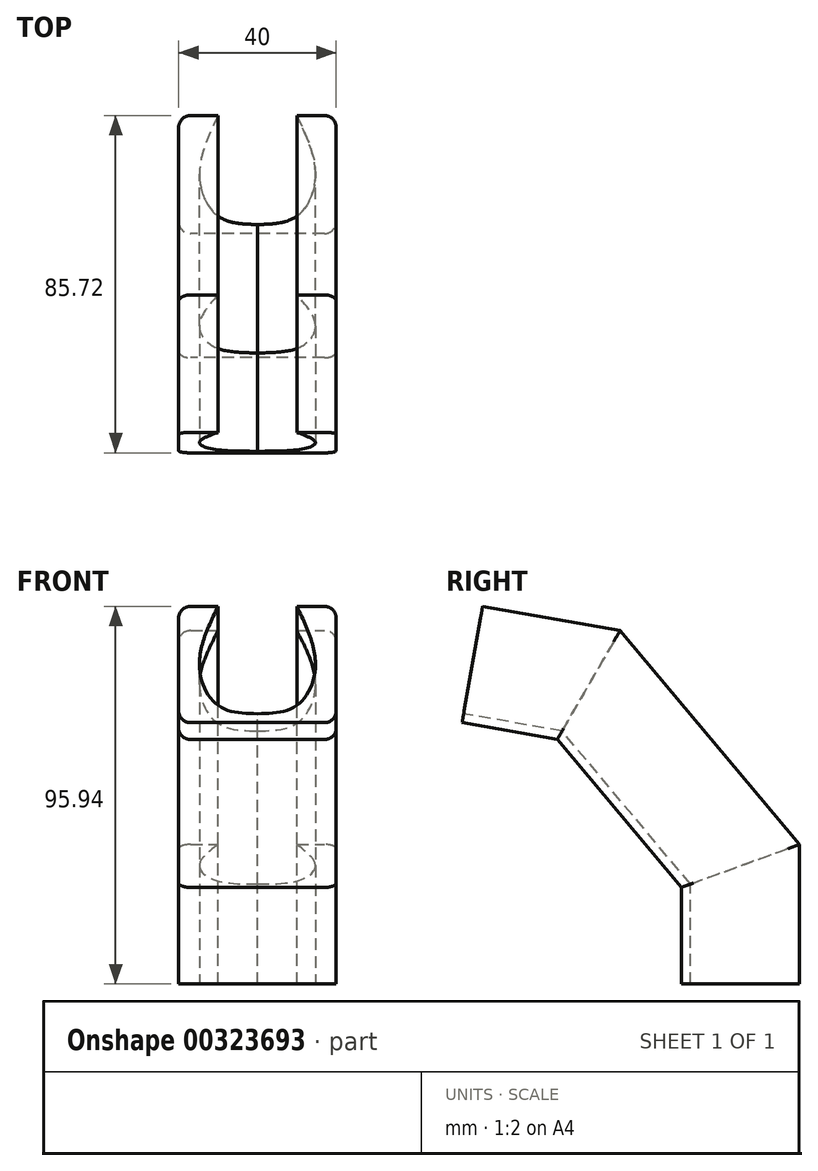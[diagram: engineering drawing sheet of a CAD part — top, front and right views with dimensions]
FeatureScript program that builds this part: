
annotation { "Feature Type Name" : "Feature", "Feature Type Description" : "" }
export const myFeature = defineFeature(function(context is Context, id is Id, definition is map)
    precondition{}
    {
        {
            var Q0;
            Q0=qCreatedBy(makeId("Top.planeOp"),FACE);
            var sketch = newSketch(context, id + "F0", { "sketchPlane" : qUnion([Q0])});
            skLineSegment(sketch, "E0.bottom", {"start": v(20, 15) * mm, "end": v(10, 15) * mm});
            skLineSegment(sketch, "E0.top", {"start": v(20, -15) * mm, "end": v(-20, -15) * mm});
            skLineSegment(sketch, "E0.left", {"start": v(20, 15) * mm, "end": v(20, -15) * mm});
            skLineSegment(sketch, "E0.right", {"start": v(-20, 15) * mm, "end": v(-20, -15) * mm});
            skPoint(sketch, "E0.middle", {"position": v(0, 0) * mm});
            skPoint(sketch, "E1", {"position": v(-10, 15) * mm});
            skPoint(sketch, "E2", {"position": v(10, 15) * mm});
            skFitSpline(sketch, "E3", {"points": [v(-10, 15) * mm, v(-14.75, 0) * mm, v(-10, -10.55) * mm, v(0, -12.7) * mm], "startDerivative": vector(-19.13, -40.12) * mm, "endDerivative": vector(36.12, -0.91) * mm});
            skFitSpline(sketch, "E4.MirrorCS", {"points": [v(10, 15) * mm, v(14.75, 0) * mm, v(10, -10.55) * mm, v(0, -12.7) * mm], "startDerivative": vector(19.13, -40.12) * mm, "endDerivative": vector(-36.12, -0.91) * mm});
            skLineSegment(sketch, "E5.trimOffspring", {"start": v(-10, 15) * mm, "end": v(-20, 15) * mm});
            skSolve(sketch);
        }
        {
            var Q0;
            Q0=qCreatedBy(makeId("Right.planeOp"),FACE);
            var sketch = newSketch(context, id + "F1", { "sketchPlane" : qUnion([Q0])});
            skLineSegment(sketch, "E6", {"start": v(0, 0) * mm, "end": v(0, 30) * mm});
            skLineSegment(sketch, "E7", {"start": v(0, 30) * mm, "end": v(-38.57, 75.96) * mm});
            skLineSegment(sketch, "E8", {"start": v(-38.57, 75.96) * mm, "end": v(-68.11, 81.17) * mm});
            skSolve(sketch);
        }
        {
            var Q0;
            Q0=makeQuery(id+"F0.imprint","IMPRINT",FACE,{"disambiguationData":[TD([[makeQuery(id+"F0.imprint","IMPRINT",EDGE,{"derivedFrom":sQuery(id+"F0.wireOp",EDGE,"E0.bottom")}),1.0]])]});
            var Q1;
            Q1=sQuery(id+"F1.wireOp",EDGE,"E6");
            var Q2;
            Q2=sQuery(id+"F1.wireOp",EDGE,"E7");
            var Q3;
            Q3=sQuery(id+"F1.wireOp",EDGE,"E8");
            sweep(context, id + "F2", {"profiles" : qUnion([Q0]), "path" : qUnion([Q1, Q2, Q3])});
        }
        {
            var Q0;
            Q0=makeQuery(id+"F2.opSweep","SWEPT_EDGE",EDGE,{"disambiguationData":[OSD([sQuery(id+"F0.wireOp",EDGE,"E0.right"),sQuery(id+"F0.wireOp",EDGE,"E5.trimOffspring"),sQuery(id+"F1.wireOp",EDGE,"E6")])]});
            var Q1;
            Q1=makeQuery(id+"F2.opSweep","SWEPT_EDGE",EDGE,{"disambiguationData":[OSD([sQuery(id+"F0.wireOp",EDGE,"E0.right"),sQuery(id+"F0.wireOp",EDGE,"E5.trimOffspring"),sQuery(id+"F1.wireOp",EDGE,"E7")])]});
            var Q2;
            Q2=makeQuery(id+"F2.opSweep","SWEPT_EDGE",EDGE,{"disambiguationData":[OSD([sQuery(id+"F0.wireOp",EDGE,"E0.right"),sQuery(id+"F0.wireOp",EDGE,"E5.trimOffspring"),sQuery(id+"F1.wireOp",EDGE,"E8")])]});
            var Q3;
            Q3=makeQuery(id+"F2.opSweep","SWEPT_EDGE",EDGE,{"disambiguationData":[OSD([sQuery(id+"F0.wireOp",EDGE,"E0.top"),sQuery(id+"F0.wireOp",EDGE,"E0.right"),sQuery(id+"F1.wireOp",EDGE,"E6")])]});
            var Q4;
            Q4=makeQuery(id+"F2.opSweep","SWEPT_EDGE",EDGE,{"disambiguationData":[OSD([sQuery(id+"F0.wireOp",EDGE,"E0.top"),sQuery(id+"F0.wireOp",EDGE,"E0.right"),sQuery(id+"F1.wireOp",EDGE,"E7")])]});
            var Q5;
            Q5=makeQuery(id+"F2.opSweep","SWEPT_EDGE",EDGE,{"disambiguationData":[OSD([sQuery(id+"F0.wireOp",EDGE,"E0.top"),sQuery(id+"F0.wireOp",EDGE,"E0.right"),sQuery(id+"F1.wireOp",EDGE,"E8")])]});
            var Q6;
            Q6=makeQuery(id+"F2.opSweep","SWEPT_EDGE",EDGE,{"disambiguationData":[OSD([sQuery(id+"F0.wireOp",EDGE,"E0.bottom"),sQuery(id+"F0.wireOp",EDGE,"E0.left"),sQuery(id+"F1.wireOp",EDGE,"E8")])]});
            var Q7;
            Q7=makeQuery(id+"F2.opSweep","SWEPT_EDGE",EDGE,{"disambiguationData":[OSD([sQuery(id+"F0.wireOp",EDGE,"E0.bottom"),sQuery(id+"F0.wireOp",EDGE,"E0.left"),sQuery(id+"F1.wireOp",EDGE,"E7")])]});
            var Q8;
            Q8=makeQuery(id+"F2.opSweep","SWEPT_EDGE",EDGE,{"disambiguationData":[OSD([sQuery(id+"F0.wireOp",EDGE,"E0.bottom"),sQuery(id+"F0.wireOp",EDGE,"E0.left"),sQuery(id+"F1.wireOp",EDGE,"E6")])]});
            var Q9;
            Q9=makeQuery(id+"F2.opSweep","SWEPT_EDGE",EDGE,{"disambiguationData":[OSD([sQuery(id+"F0.wireOp",EDGE,"E0.top"),sQuery(id+"F0.wireOp",EDGE,"E0.left"),sQuery(id+"F1.wireOp",EDGE,"E6")])]});
            var Q10;
            Q10=makeQuery(id+"F2.opSweep","SWEPT_EDGE",EDGE,{"disambiguationData":[OSD([sQuery(id+"F0.wireOp",EDGE,"E0.top"),sQuery(id+"F0.wireOp",EDGE,"E0.left"),sQuery(id+"F1.wireOp",EDGE,"E7")])]});
            var Q11;
            Q11=makeQuery(id+"F2.opSweep","SWEPT_EDGE",EDGE,{"disambiguationData":[OSD([sQuery(id+"F0.wireOp",EDGE,"E0.top"),sQuery(id+"F0.wireOp",EDGE,"E0.left"),sQuery(id+"F1.wireOp",EDGE,"E8")])]});
            fillet(context, id + "F3", {"entities" : qUnion([Q0, Q1, Q2, Q3, Q4, Q5, Q6, Q7, Q8, Q9, Q10, Q11]), "radius" : 3 * mm, "tangentPropagation" : true, "allowEdgeOverflow" : false});
        }
    });
